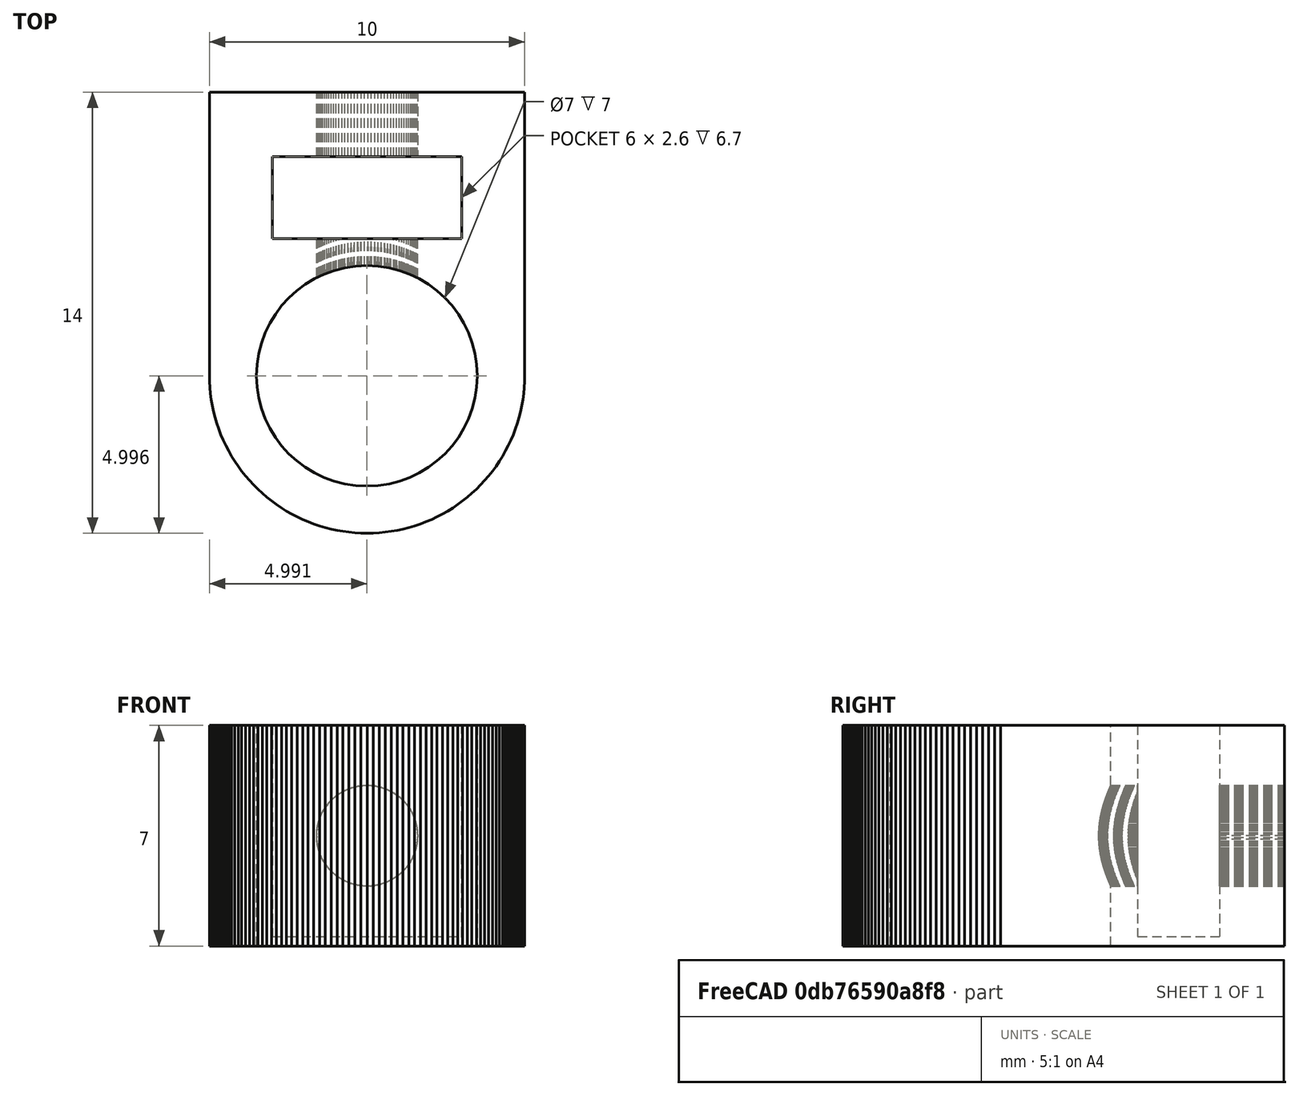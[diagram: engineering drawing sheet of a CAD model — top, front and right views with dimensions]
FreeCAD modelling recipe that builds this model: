
FCSTD DOCUMENT  (FreeCAD 0.18R4 (GitTag))
Label: Plastic
License: All rights reserved
LicenseURL: http://en.wikipedia.org/wiki/All_rights_reserved
objects: Part::Feature×3, Mesh::Feature×1, Sketcher::SketchObject×1, Part::Extrusion×1, Part::Cut×1
note: 6 computed .brp shape members not serialized (recipe doc carries the construction recipe); baked Part::Feature solids carry a one-line shape summary decoded from their .brp

FEATURE [Mesh::Feature] Side_Panel_Column
FEATURE [Part::Feature] Side_Panel_Column001
  shape: bbox 10 x 14 x 7 mm, 2276 faces, 0 solids (baked)
FEATURE [Part::Feature] Side_Panel_Column001001  label="Side_Panel_Column002"
  shape: bbox 10 x 14 x 7 mm, 719 faces, 0 solids (baked)
FEATURE [Sketcher::SketchObject] Sketch
  MapMode = 5
  Placement = pos=(0,0,7) rot=(0,0,1;0rad)
  Support = -> [Side_Panel_Column001001]
  sketch-geometry (1):
    g0: Circle CenterX=-64.7486 CenterY=62.0662 CenterZ=0 NormalX=0 NormalY=0 NormalZ=1 AngleXU=0 Radius=3.5
  constraints (1):
    c: Radius(g0) = 3.5
FEATURE [Part::Extrusion] Extrude
  Base = -> Sketch
  Dir = (0,0,1)
  DirMode = 2
  FaceMakerClass = Part::FaceMakerBullseye
  LengthFwd = -100
  LengthRev = 0
  Solid = true
  Symmetric = true
FEATURE [Part::Feature] Side_Panel_Column001001_solid  label="Side_Panel_Column002 (Solid)"
  shape: bbox 10 x 14 x 7 mm, 719 faces (baked)
FEATURE [Part::Cut] Cut
  Base = -> Side_Panel_Column001001_solid
  Tool = -> Extrude
